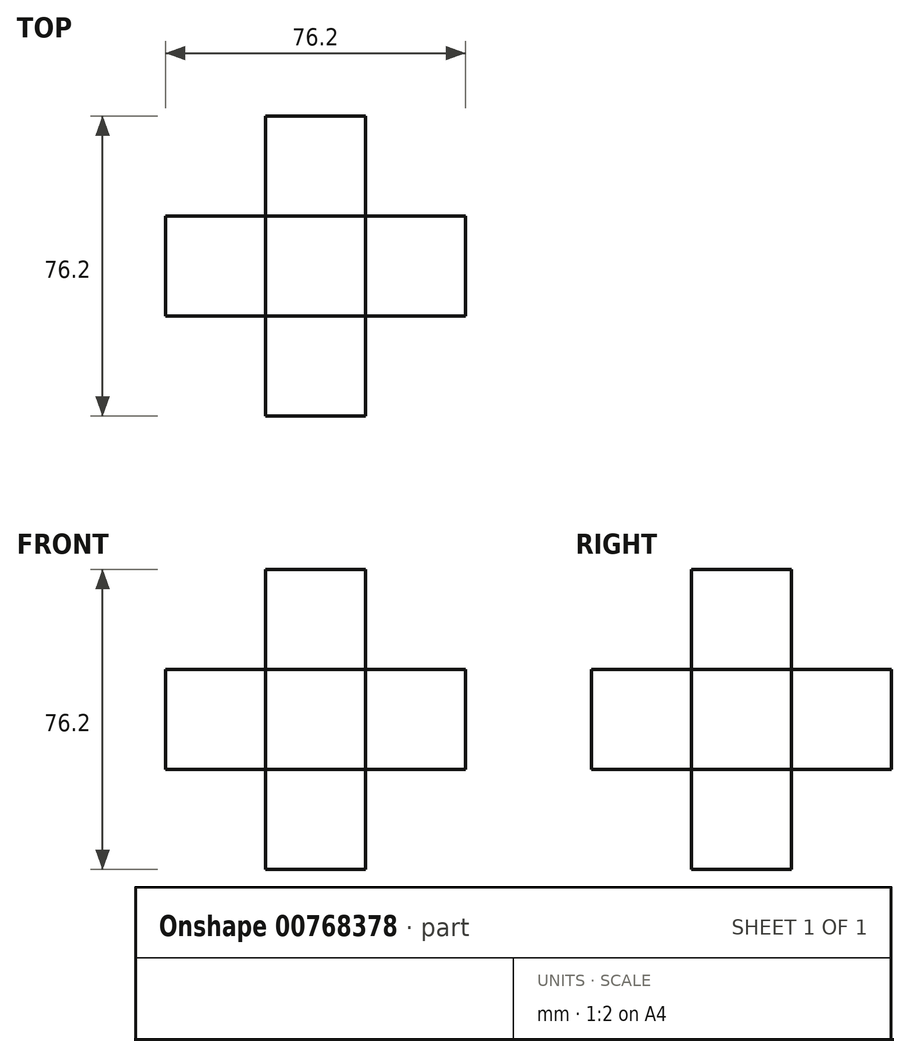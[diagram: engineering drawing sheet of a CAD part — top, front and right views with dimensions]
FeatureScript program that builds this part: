
annotation { "Feature Type Name" : "Feature", "Feature Type Description" : "" }
export const myFeature = defineFeature(function(context is Context, id is Id, definition is map)
    precondition{}
    {
        {
            var Q0;
            Q0=qCreatedBy(makeId("Top.planeOp"),FACE);
            var sketch = newSketch(context, id + "F0", { "sketchPlane" : qUnion([Q0])});
            skCircle(sketch, "E0", {"center": v(-42.82, -23.48) * mm, "radius": 13.99 * mm});
            skSolve(sketch);
        }
        {
            var Q0;
            Q0=makeQuery(id+"F0.imprint","IMPRINT",FACE,{"disambiguationData":[TD([[makeQuery(id+"F0.imprint","IMPRINT",EDGE,{"derivedFrom":sQuery(id+"F0.wireOp",EDGE,"E0")}),1.0]])]});
            extrude(context, id + "F1", {"entities" : qUnion([Q0]), "depth" : 25.4 * mm, "offsetDistance" : 25.4 * mm});
        }
        {
            var Q0;
            Q0=makeQuery(id+"F1.opExtrude","SWEPT_FACE",FACE,{"disambiguationData":[OSD([sQuery(id+"F0.wireOp",EDGE,"E0")])]});
            chamfer(context, id + "F2", {"entities" : qUnion([Q0]), "width" : 12.7 * mm, "tangentPropagation" : true});
        }
        {
            var Q0;
            Q0=qCreatedBy(makeId("Top.planeOp"),FACE);
            var sketch = newSketch(context, id + "F3", { "sketchPlane" : qUnion([Q0])});
            skLineSegment(sketch, "E1.bottom", {"start": v(16.37, 41.68) * mm, "end": v(92.57, 41.68) * mm});
            skLineSegment(sketch, "E1.top", {"start": v(16.37, -34.52) * mm, "end": v(92.57, -34.52) * mm});
            skLineSegment(sketch, "E1.left", {"start": v(16.37, 41.68) * mm, "end": v(16.37, -34.52) * mm});
            skLineSegment(sketch, "E1.right", {"start": v(92.57, 41.68) * mm, "end": v(92.57, -34.52) * mm});
            skSolve(sketch);
        }
        {
            var Q0;
            Q0=makeQuery(id+"F3.imprint","IMPRINT",FACE,{"disambiguationData":[TD([[makeQuery(id+"F3.imprint","IMPRINT",EDGE,{"derivedFrom":sQuery(id+"F3.wireOp",EDGE,"E1.bottom")}),-1.0]])]});
            extrude(context, id + "F4", {"entities" : qUnion([Q0]), "depth" : 76.2 * mm, "offsetDistance" : 25.4 * mm});
        }
        {
            var Q0;
            Q0=makeQuery(id+"F4.opExtrude","SWEPT_FACE",FACE,{"disambiguationData":[OSD([sQuery(id+"F3.wireOp",EDGE,"E1.top")])]});
            var sketch = newSketch(context, id + "F5", { "sketchPlane" : qUnion([Q0])});
            skLineSegment(sketch, "E2.bottom", {"start": v(16.37, 76.2) * mm, "end": v(41.77, 76.2) * mm});
            skLineSegment(sketch, "E2.top", {"start": v(16.37, 50.8) * mm, "end": v(41.77, 50.8) * mm});
            skLineSegment(sketch, "E2.left", {"start": v(16.37, 76.2) * mm, "end": v(16.37, 50.8) * mm});
            skLineSegment(sketch, "E2.right", {"start": v(41.77, 76.2) * mm, "end": v(41.77, 50.8) * mm});
            skLineSegment(sketch, "E3.bottom", {"start": v(16.37, 76.2) * mm, "end": v(67.17, 76.2) * mm});
            skLineSegment(sketch, "E3.top", {"start": v(16.37, 25.4) * mm, "end": v(67.17, 25.4) * mm});
            skLineSegment(sketch, "E3.left", {"start": v(16.37, 76.2) * mm, "end": v(16.37, 25.4) * mm});
            skLineSegment(sketch, "E3.right", {"start": v(67.17, 76.2) * mm, "end": v(67.17, 25.4) * mm});
            skLineSegment(sketch, "E4", {"start": v(16.37, 50.8) * mm, "end": v(92.57, 50.8) * mm});
            skLineSegment(sketch, "E5", {"start": v(92.57, 50.8) * mm, "end": v(92.57, 25.4) * mm});
            skLineSegment(sketch, "E6", {"start": v(92.57, 25.4) * mm, "end": v(16.37, 25.4) * mm});
            skLineSegment(sketch, "E7", {"start": v(41.77, 50.8) * mm, "end": v(41.77, 0) * mm});
            skLineSegment(sketch, "E8", {"start": v(67.17, 25.4) * mm, "end": v(67.17, 0) * mm});
            skSolve(sketch);
        }
        {
            var Q0;
            Q0=makeQuery(id+"F1.opExtrude","SWEPT_BODY",BODY,{"disambiguationData":[OSD([sQuery(id+"F0.wireOp",EDGE,"E0")])]});
            deleteBodies(context, id + "F6", {"entities" : qUnion([Q0])});
        }
        {
            var Q0;
            {var subQ0=sQuery(id+"F5.wireOp",EDGE,"E2.right");Q0=makeQuery(id+"F5.imprint","IMPRINT",FACE,{"disambiguationData":[TD([[makeQuery(id+"F5.imprint","IMPRINT",EDGE,{"derivedFrom":subQ0}),-1.0]])]});}
            var Q1;
            {var subQ0=sQuery(id+"F5.wireOp",EDGE,"E3.right");var subQ4=sQuery(id+"F5.wireOp",EDGE,"E4");var subQ5=makeQuery(id+"F5.imprint","INTERSECT",VERTEX,{"derivedFrom":[subQ0,subQ4]});Q1=makeQuery(id+"F5.imprint","IMPRINT",FACE,{"disambiguationData":[TD([[makeQuery(id+"F5.imprint","IMPRINT",EDGE,{"disambiguationData":[TD([[subQ5,1.0]])],"derivedFrom":subQ0}),1.0]])]});}
            var Q2;
            {var subQ0=sQuery(id+"F5.wireOp",EDGE,"E8");Q2=makeQuery(id+"F5.imprint","IMPRINT",FACE,{"disambiguationData":[TD([[makeQuery(id+"F5.imprint","IMPRINT",EDGE,{"derivedFrom":subQ0}),1.0]])]});}
            var Q3;
            {var subQ1=sQuery(id+"F3.wireOp",EDGE,"E1.top");var subQ4=sQuery(id+"F5.wireOp",EDGE,"E7");var subQ6=makeQuery(id+"F4.opExtrude","CAP_EDGE",EDGE,{"disambiguationData":[OSD([subQ1])],"isStart":true});var subQ7=makeQuery(id+"F5.imprint","INTERSECT",VERTEX,{"derivedFrom":[subQ6,subQ4]});Q3=makeQuery(id+"F5.imprint","IMPRINT",FACE,{"disambiguationData":[TD([[makeQuery(id+"F5.imprint","IMPRINT",EDGE,{"disambiguationData":[TD([[subQ7,1.0]])],"derivedFrom":subQ4}),-1.0]])]});}
            extrude(context, id + "F7", {"entities" : qUnion([Q0, Q1, Q2, Q3]), "operationType" : NewBodyOperationType.REMOVE, "oppositeDirection" : true, "depth" : 76.2 * mm, "offsetDistance" : 25.4 * mm});
        }
        {
            var Q0;
            Q0=makeQuery(id+"F4.opExtrude","SWEPT_FACE",FACE,{"disambiguationData":[OSD([sQuery(id+"F3.wireOp",EDGE,"E1.right")])]});
            var sketch = newSketch(context, id + "F8", { "sketchPlane" : qUnion([Q0])});
            skLineSegment(sketch, "E9.bottom", {"start": v(-34.52, 50.8) * mm, "end": v(-9.12, 50.8) * mm});
            skLineSegment(sketch, "E9.top", {"start": v(-34.52, 76.2) * mm, "end": v(-9.12, 76.2) * mm});
            skLineSegment(sketch, "E9.left", {"start": v(-34.52, 50.8) * mm, "end": v(-34.52, 76.2) * mm});
            skLineSegment(sketch, "E9.right", {"start": v(-9.12, 50.8) * mm, "end": v(-9.12, 76.2) * mm});
            skLineSegment(sketch, "E10.bottom", {"start": v(41.68, 50.8) * mm, "end": v(16.28, 50.8) * mm});
            skLineSegment(sketch, "E10.top", {"start": v(41.68, 76.2) * mm, "end": v(16.28, 76.2) * mm});
            skLineSegment(sketch, "E10.left", {"start": v(41.68, 50.8) * mm, "end": v(41.68, 76.2) * mm});
            skLineSegment(sketch, "E10.right", {"start": v(16.28, 50.8) * mm, "end": v(16.28, 76.2) * mm});
            skLineSegment(sketch, "E11.bottom", {"start": v(-34.52, 25.4) * mm, "end": v(-9.12, 25.4) * mm});
            skLineSegment(sketch, "E11.top", {"start": v(-34.52, 0) * mm, "end": v(-9.12, 0) * mm});
            skLineSegment(sketch, "E11.left", {"start": v(-34.52, 25.4) * mm, "end": v(-34.52, 0) * mm});
            skLineSegment(sketch, "E11.right", {"start": v(-9.12, 25.4) * mm, "end": v(-9.12, 0) * mm});
            skLineSegment(sketch, "E12.bottom", {"start": v(41.68, 25.4) * mm, "end": v(16.28, 25.4) * mm});
            skLineSegment(sketch, "E12.top", {"start": v(41.68, 0) * mm, "end": v(16.28, 0) * mm});
            skLineSegment(sketch, "E12.left", {"start": v(41.68, 25.4) * mm, "end": v(41.68, 0) * mm});
            skLineSegment(sketch, "E12.right", {"start": v(16.28, 25.4) * mm, "end": v(16.28, 0) * mm});
            skSolve(sketch);
        }
        {
            var Q0;
            Q0=makeQuery(id+"F8.imprint","IMPRINT",FACE,{"disambiguationData":[TD([[makeQuery(id+"F8.imprint","IMPRINT",EDGE,{"derivedFrom":sQuery(id+"F8.wireOp",EDGE,"E11.bottom")}),1.0]])]});
            var Q1;
            Q1=makeQuery(id+"F8.imprint","IMPRINT",FACE,{"disambiguationData":[TD([[makeQuery(id+"F8.imprint","IMPRINT",EDGE,{"derivedFrom":sQuery(id+"F8.wireOp",EDGE,"E9.bottom")}),-1.0]])]});
            var Q2;
            Q2=makeQuery(id+"F8.imprint","IMPRINT",FACE,{"disambiguationData":[TD([[makeQuery(id+"F8.imprint","IMPRINT",EDGE,{"derivedFrom":sQuery(id+"F8.wireOp",EDGE,"E10.bottom")}),-1.0]])]});
            var Q3;
            Q3=makeQuery(id+"F8.imprint","IMPRINT",FACE,{"disambiguationData":[TD([[makeQuery(id+"F8.imprint","IMPRINT",EDGE,{"derivedFrom":sQuery(id+"F8.wireOp",EDGE,"E12.bottom")}),1.0]])]});
            extrude(context, id + "F9", {"entities" : qUnion([Q0, Q1, Q2, Q3]), "operationType" : NewBodyOperationType.REMOVE, "oppositeDirection" : true, "depth" : 76.2 * mm, "offsetDistance" : 25.4 * mm});
        }
        {
            var Q0;
            {var subQ0=sQuery(id+"F5.wireOp",EDGE,"E4");Q0=makeQuery(id+"F9.boolean.opBoolean","MERGE",FACE,{"derivedFrom":[makeQuery(id+"F7.boolean.opBoolean","COPY",FACE,{"derivedFrom":makeQuery(id+"F7.opExtrude","SWEPT_FACE",FACE,{"disambiguationData":[OSD([subQ0]),TDD([makeQuery(id+"F5.imprint","IMPRINT",EDGE,{"disambiguationData":[TD([[makeQuery(id+"F5.imprint","INTERSECT",VERTEX,{"derivedFrom":[sQuery(id+"F5.wireOp",EDGE,"E3.left"),subQ0]}),-1.0]])],"derivedFrom":subQ0})])]})}),makeQuery(id+"F7.boolean.opBoolean","COPY",FACE,{"derivedFrom":makeQuery(id+"F7.opExtrude","SWEPT_FACE",FACE,{"disambiguationData":[OSD([subQ0]),TDD([makeQuery(id+"F5.imprint","IMPRINT",EDGE,{"disambiguationData":[TD([[makeQuery(id+"F5.imprint","INTERSECT",VERTEX,{"derivedFrom":[sQuery(id+"F5.wireOp",EDGE,"E3.right"),subQ0]}),-1.0]])],"derivedFrom":subQ0})])]})}),makeQuery(id+"F9.opExtrude","SWEPT_FACE",FACE,{"disambiguationData":[OSD([sQuery(id+"F8.wireOp",EDGE,"E9.bottom")])]}),makeQuery(id+"F9.opExtrude","SWEPT_FACE",FACE,{"disambiguationData":[OSD([sQuery(id+"F8.wireOp",EDGE,"E10.bottom")])]})]});}
            var sketch = newSketch(context, id + "F10", { "sketchPlane" : qUnion([Q0])});
            skLineSegment(sketch, "E13.bottom", {"start": v(92.57, -34.52) * mm, "end": v(67.17, -34.52) * mm});
            skLineSegment(sketch, "E13.top", {"start": v(92.57, -9.12) * mm, "end": v(67.17, -9.12) * mm});
            skLineSegment(sketch, "E13.left", {"start": v(92.57, -34.52) * mm, "end": v(92.57, -9.12) * mm});
            skLineSegment(sketch, "E13.right", {"start": v(67.17, -34.52) * mm, "end": v(67.17, -9.12) * mm});
            skLineSegment(sketch, "E14.bottom", {"start": v(67.17, 16.28) * mm, "end": v(92.57, 16.28) * mm});
            skLineSegment(sketch, "E14.top", {"start": v(67.17, 41.68) * mm, "end": v(92.57, 41.68) * mm});
            skLineSegment(sketch, "E14.left", {"start": v(67.17, 16.28) * mm, "end": v(67.17, 41.68) * mm});
            skLineSegment(sketch, "E14.right", {"start": v(92.57, 16.28) * mm, "end": v(92.57, 41.68) * mm});
            skLineSegment(sketch, "E15.bottom", {"start": v(41.77, 16.28) * mm, "end": v(16.37, 16.28) * mm});
            skLineSegment(sketch, "E15.top", {"start": v(41.77, 41.68) * mm, "end": v(16.37, 41.68) * mm});
            skLineSegment(sketch, "E15.left", {"start": v(41.77, 16.28) * mm, "end": v(41.77, 41.68) * mm});
            skLineSegment(sketch, "E15.right", {"start": v(16.37, 16.28) * mm, "end": v(16.37, 41.68) * mm});
            skLineSegment(sketch, "E16.bottom", {"start": v(41.77, -9.12) * mm, "end": v(16.37, -9.12) * mm});
            skLineSegment(sketch, "E16.top", {"start": v(41.77, -34.52) * mm, "end": v(16.37, -34.52) * mm});
            skLineSegment(sketch, "E16.left", {"start": v(41.77, -9.12) * mm, "end": v(41.77, -34.52) * mm});
            skLineSegment(sketch, "E16.right", {"start": v(16.37, -9.12) * mm, "end": v(16.37, -34.52) * mm});
            skSolve(sketch);
        }
        {
            var Q0;
            Q0=qSketchRegion(id+"F10",true);
            extrude(context, id + "F11", {"entities" : qUnion([Q0]), "operationType" : NewBodyOperationType.REMOVE, "oppositeDirection" : true, "depth" : 76.2 * mm, "offsetDistance" : 25.4 * mm});
        }
    });
